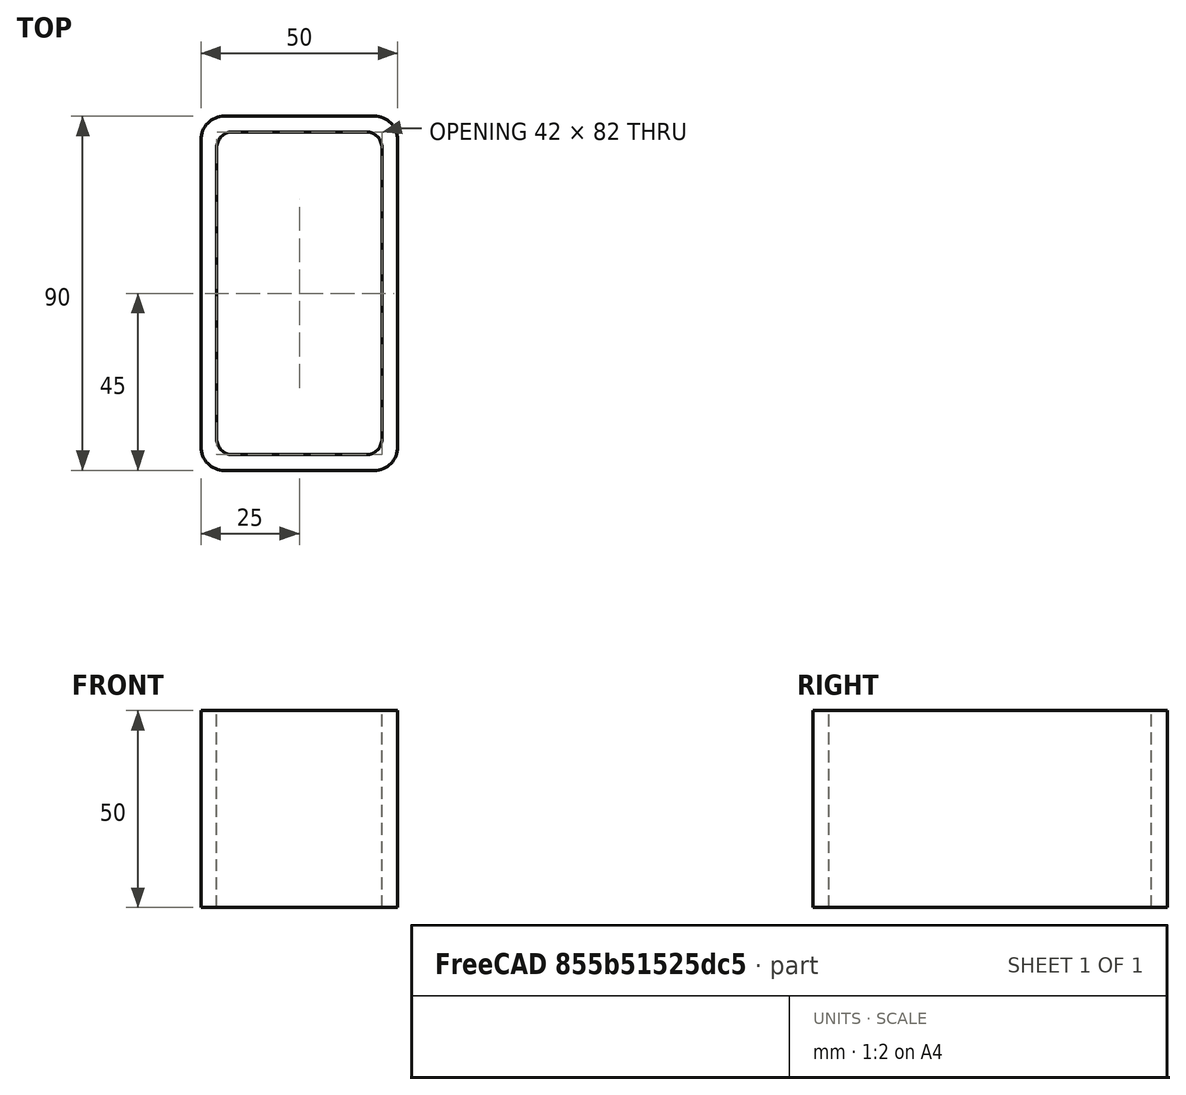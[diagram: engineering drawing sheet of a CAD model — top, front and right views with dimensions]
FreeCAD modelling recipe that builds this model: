
FCSTD DOCUMENT  (FreeCAD 0.15R4671 (Git))
Label: Rectangular hollow section 90x50x4 EN10219 S235JRH
License: All rights reserved
LicenseURL: http://en.wikipedia.org/wiki/All_rights_reserved
objects: Sketcher::SketchObject×1, Part::Extrusion×1
note: 2 computed .brp shape members not serialized (recipe doc carries the construction recipe); baked Part::Feature solids carry a one-line shape summary decoded from their .brp

FEATURE [Sketcher::SketchObject] Sketch
  sketch-geometry (16):
    g0: LineSegment StartX=-17 StartY=41 StartZ=0 EndX=17 EndY=41 EndZ=0
    g1: LineSegment StartX=21 StartY=37 StartZ=0 EndX=21 EndY=-37 EndZ=0
    g2: LineSegment StartX=17 StartY=-41 StartZ=0 EndX=-17 EndY=-41 EndZ=0
    g3: LineSegment StartX=-21 StartY=-37 StartZ=0 EndX=-21 EndY=37 EndZ=0
    g4: LineSegment StartX=-19 StartY=45 StartZ=0 EndX=19 EndY=45 EndZ=0
    g5: LineSegment StartX=25 StartY=39 StartZ=0 EndX=25 EndY=-39 EndZ=0
    g6: LineSegment StartX=19 StartY=-45 StartZ=0 EndX=-19 EndY=-45 EndZ=0
    g7: LineSegment StartX=-25 StartY=-39 StartZ=0 EndX=-25 EndY=39 EndZ=0
    g8: ArcOfCircle CenterX=-17 CenterY=37 CenterZ=0 NormalX=0 NormalY=0 NormalZ=1 Radius=4 StartAngle=1.5708 EndAngle=3.14159
    g9: ArcOfCircle CenterX=17 CenterY=37 CenterZ=0 NormalX=0 NormalY=0 NormalZ=1 Radius=4 StartAngle=0 EndAngle=1.5708
    g10: ArcOfCircle CenterX=17 CenterY=-37 CenterZ=0 NormalX=0 NormalY=0 NormalZ=1 Radius=4 StartAngle=4.71239 EndAngle=6.28319
    g11: ArcOfCircle CenterX=-17 CenterY=-37 CenterZ=0 NormalX=0 NormalY=0 NormalZ=1 Radius=4 StartAngle=3.14159 EndAngle=4.71239
    g12: ArcOfCircle CenterX=19 CenterY=39 CenterZ=0 NormalX=0 NormalY=0 NormalZ=1 Radius=6 StartAngle=0 EndAngle=1.5708
    g13: ArcOfCircle CenterX=19 CenterY=-39 CenterZ=0 NormalX=0 NormalY=0 NormalZ=1 Radius=6 StartAngle=4.71239 EndAngle=6.28319
    g14: ArcOfCircle CenterX=-19 CenterY=-39 CenterZ=0 NormalX=0 NormalY=0 NormalZ=1 Radius=6 StartAngle=3.14159 EndAngle=4.71239
    g15: ArcOfCircle CenterX=-19 CenterY=39 CenterZ=0 NormalX=0 NormalY=0 NormalZ=1 Radius=6 StartAngle=1.5708 EndAngle=3.14159
  constraints (36):
    c: Horizontal(g2)
    c: Vertical(g3)
    c: Horizontal(g6)
    c: Vertical(g7)
    c: Tangent(g3,g8) = 1.5708
    c: Tangent(g0,g8) = 1.5708
    c: Tangent(g0,g9) = 1.5708
    c: Tangent(g1,g9) = 1.5708
    c: Tangent(g1,g10) = 1.5708
    c: Tangent(g2,g10) = 1.5708
    c: Tangent(g2,g11) = 1.5708
    c: Tangent(g3,g11) = 1.5708
    c: Tangent(g4,g12) = 1.5708
    c: Tangent(g5,g12) = 1.5708
    c: Tangent(g5,g13) = 1.5708
    c: Tangent(g6,g13) = 1.5708
    c: Tangent(g6,g14) = 1.5708
    c: Tangent(g7,g14) = 1.5708
    c: Tangent(g7,g15) = 1.5708
    c: Tangent(g4,g15) = 1.5708
    c: Equal(g9,g8)
    c: Equal(g9,g11)
    c: Equal(g9,g10)
    c: Equal(g12,g15)
    c: Equal(g12,g14)
    c: Equal(g12,g13)
    c: Symmetric(g4,g6,g-1)
    c: Symmetric(g7,g5,g-2)
    c: DistanceY(g4,g6) = -90
    c: DistanceX(g7,g5) = 50
    c: Symmetric(g3,g1,g-2)
    c: Symmetric(g0,g2,g-1)
    c: DistanceY(g0,g4) = 4
    c: DistanceX(g5,g1) = -4
    c: Radius(g9) = 4
    c: Radius(g12) = 6
FEATURE [Part::Extrusion] Extrude  label="Rectangular hollow section 90x50x4 EN10219 S235JRH"
  Base = -> Sketch
  Dir = (0,0,50)
  Solid = true
